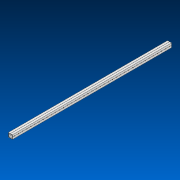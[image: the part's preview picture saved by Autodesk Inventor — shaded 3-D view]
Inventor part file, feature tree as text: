
AUTODESK INVENTOR PART (.ipt)
format: ipt  version: 2022.2 (Build 262287000, 287)  size: 823,296 bytes
history: native  units: in
note: dims shown in document units (in); Inventor stores cm internally (conversion verified against a paired STEP export)
features: other x39, extrude x1, pattern_linear x1, sketch x1, pattern_circular x1
ambient origin geometry x8: Origin, YZ Plane, XZ Plane, XY Plane, X Axis, Y Axis, Z Axis, Center Point
bodies: Solid1 (feature_tree)
feature tree (43):
  extrude  "Extrusion1"  Depth=1.0in
  other  "Work Axis1"
  pattern_linear  "Rectangular Pattern1"  Spacing1=0.0in  [1 undecoded]
  sketch  "Sketch1"  dims[d0=1.0in d1=20.0in d2=0.0in d3=15.3543in d5=1.0in]
  other  "Work Axis2"
  other  "Work Axis3"
  other  "Work Axis4"
  other  "Work Axis5"
  other  "Work Axis6"
  other  "Work Axis7"
  other  "Work Axis8"
  other  "Work Axis9"
  other  "Work Axis10"
  other  "Work Axis11"
  other  "Work Axis12"
  other  "Work Axis13"
  other  "Work Axis14"
  other  "Work Axis15"
  other  "Work Axis16"
  other  "Work Axis17"
  other  "Work Axis18"
  other  "Work Axis19"
  other  "Work Axis20"
  other  "Work Axis21"
  other  "Work Axis22"
  other  "Work Axis23"
  other  "Work Axis24"
  other  "Work Axis25"
  other  "Work Axis26"
  other  "Work Axis27"
  other  "Work Axis28"
  other  "Work Axis29"
  other  "Work Axis30"
  other  "Work Axis31"
  other  "Work Axis32"
  other  "Work Axis33"
  other  "Work Axis34"
  other  "Work Axis35"
  other  "Work Axis36"
  other  "Work Axis37"
  other  "Work Axis38"
  other  "Work Axis39"
  pattern_circular  "CirPattern2"
note: 1 required parameter value undecoded (feature->parameter linkage not recoverable at this tier; creation-order binding heuristic only, values carry confidence <= 0.55)
